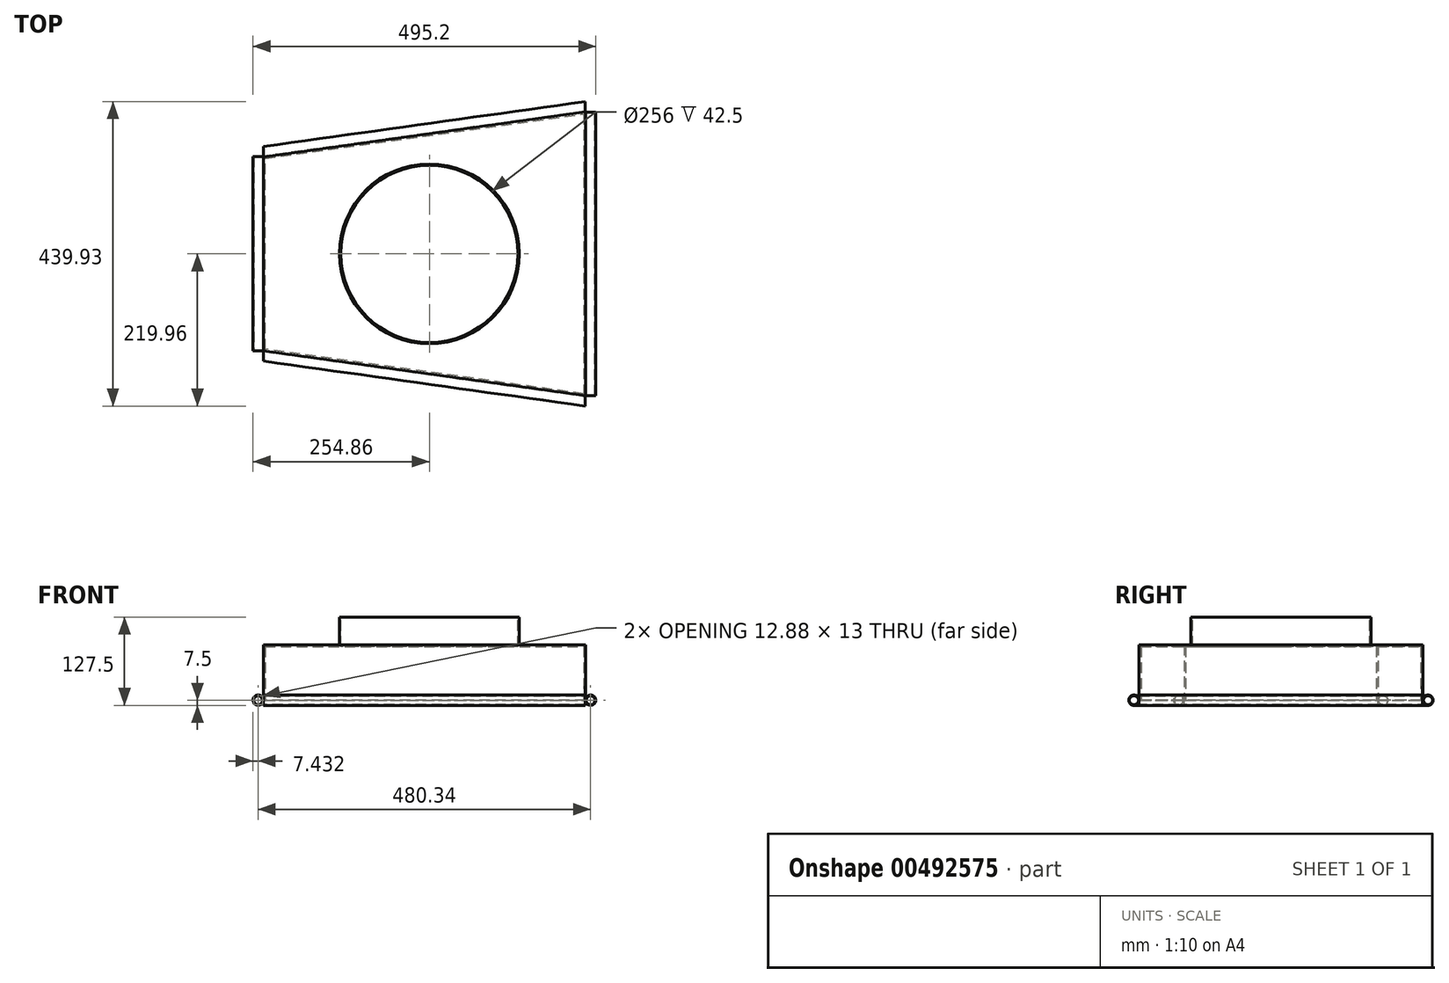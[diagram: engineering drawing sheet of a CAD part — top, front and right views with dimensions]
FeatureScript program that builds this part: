
annotation { "Feature Type Name" : "Feature", "Feature Type Description" : "" }
export const myFeature = defineFeature(function(context is Context, id is Id, definition is map)
    precondition{}
    {
        {
            var Q0;
            Q0=qCreatedBy(makeId("Top.planeOp"),FACE);
            var sketch = newSketch(context, id + "F0", { "sketchPlane" : qUnion([Q0])});
            skLineSegment(sketch, "E0", {"start": v(0, 0) * mm, "end": v(0, 280) * mm});
            skLineSegment(sketch, "E1", {"start": v(0, 140) * mm, "end": v(465.48, 140) * mm, "construction": true});
            skLineSegment(sketch, "E2", {"start": v(465.48, 345) * mm, "end": v(465.48, -65) * mm});
            skLineSegment(sketch, "E3", {"start": v(0, 280) * mm, "end": v(465.48, 345) * mm});
            skLineSegment(sketch, "E4", {"start": v(465.48, -65) * mm, "end": v(0, 0) * mm});
            skSolve(sketch);
        }
        {
            var Q0;
            Q0 = qSketchRegion(id + "F0", true);
            extrude(context, id + "F1", {"entities" : qUnion([Q0]), "depth" : 80 * mm, "offsetDistance" : 25 * mm});
        }
        {
            var Q0;
            Q0=makeQuery(id+"F1.opExtrude","CAP_FACE",FACE,{"disambiguationData":[OSD([sQuery(id+"F0.wireOp",EDGE,"E0"),sQuery(id+"F0.wireOp",EDGE,"E2"),sQuery(id+"F0.wireOp",EDGE,"E3"),sQuery(id+"F0.wireOp",EDGE,"E4")])],"isStart":false});
            var sketch = newSketch(context, id + "F2", { "sketchPlane" : qUnion([Q0])});
            skCircle(sketch, "E5", {"center": v(240, 140) * mm, "radius": 130 * mm});
            skLineSegment(sketch, "E6", {"start": v(465.48, 140) * mm, "end": v(0, 140) * mm, "construction": true});
            skSolve(sketch);
        }
        {
            var Q0;
            Q0 = qSketchRegion(id + "F2", true);
            extrude(context, id + "F3", {"entities" : qUnion([Q0]), "operationType" : NewBodyOperationType.ADD, "depth" : 40 * mm, "offsetDistance" : 25 * mm});
        }
        {
            var Q0;
            Q0=makeQuery(id+"F1.opExtrude","CAP_FACE",FACE,{"disambiguationData":[OSD([sQuery(id+"F0.wireOp",EDGE,"E0"),sQuery(id+"F0.wireOp",EDGE,"E2"),sQuery(id+"F0.wireOp",EDGE,"E3"),sQuery(id+"F0.wireOp",EDGE,"E4")])],"isStart":true});
            shell(context, id + "F4", {"entities" : qUnion([Q0]), "thickness" : 2.5 * mm});
        }
        {
            var Q0;
            Q0=makeQuery(id+"F3.opExtrude","CAP_FACE",FACE,{"disambiguationData":[OSD([sQuery(id+"F2.wireOp",EDGE,"E5")])],"isStart":false});
            var sketch = newSketch(context, id + "F5", { "sketchPlane" : qUnion([Q0])});
            skCircle(sketch, "E7.0", {"center": v(240, 140) * mm, "radius": 128 * mm});
            skSolve(sketch);
        }
        {
            var Q0;
            Q0 = qSketchRegion(id + "F5", true);
            var Q1;
            Q1=makeQuery(id+"F4.opShell","OFFSET_FACE",FACE,{"disambiguationData":[OSD([sQuery(id+"F0.wireOp",EDGE,"E0"),sQuery(id+"F0.wireOp",EDGE,"E2"),sQuery(id+"F0.wireOp",EDGE,"E3"),sQuery(id+"F0.wireOp",EDGE,"E4")])]});
            extrude(context, id + "F6", {"entities" : qUnion([Q0]), "operationType" : NewBodyOperationType.REMOVE, "endBound" : BoundingType.UP_TO_SURFACE, "oppositeDirection" : true, "depth" : 25 * mm, "endBoundEntityFace" : qUnion([Q1]), "offsetDistance" : 25 * mm});
        }
        {
            var Q0;
            Q0=makeQuery(id+"F1.opExtrude","SWEPT_FACE",FACE,{"disambiguationData":[OSD([sQuery(id+"F0.wireOp",EDGE,"E2")])]});
            var sketch = newSketch(context, id + "F7", { "sketchPlane" : qUnion([Q0])});
            skLineSegment(sketch, "E8", {"start": v(-65, 0) * mm, "end": v(-80, 0) * mm, "construction": true});
            skCircle(sketch, "E9", {"center": v(-72.5, 0) * mm, "radius": 7.5 * mm});
            skCircle(sketch, "E10.0", {"center": v(-72.5, 0) * mm, "radius": 6.5 * mm});
            skSolve(sketch);
        }
        {
            var Q0;
            Q0=qCreatedBy(makeId("Top.planeOp"),FACE);
            var sketch = newSketch(context, id + "F8", { "sketchPlane" : qUnion([Q0])});
            skLineSegment(sketch, "E11.0", {"start": v(-8, 286.96) * mm, "end": v(473.48, 354.2) * mm});
            skLineSegment(sketch, "E11.1", {"start": v(-8, -6.96) * mm, "end": v(-8, 286.96) * mm});
            skLineSegment(sketch, "E11.2", {"start": v(473.48, -74.2) * mm, "end": v(-8, -6.96) * mm});
            skLineSegment(sketch, "E11.3", {"start": v(473.48, 354.2) * mm, "end": v(473.48, -74.2) * mm});
            skSolve(sketch);
        }
        {
            var Q0;
            Q0=makeQuery(id+"F7.imprint","IMPRINT",FACE,{"disambiguationData":[TD([[makeQuery(id+"F7.imprint","IMPRINT",EDGE,{"derivedFrom":sQuery(id+"F7.wireOp",EDGE,"E9")}),1.0]])]});
            var Q1;
            Q1=sQuery(id+"F8.wireOp",EDGE,"E11.2");
            var Q2;
            Q2=sQuery(id+"F8.wireOp",EDGE,"E11.1");
            var Q3;
            Q3=sQuery(id+"F8.wireOp",EDGE,"E11.0");
            var Q4;
            Q4=sQuery(id+"F8.wireOp",EDGE,"E11.3");
            sweep(context, id + "F9", {"profiles" : qUnion([Q0]), "path" : qUnion([Q1, Q2, Q3, Q4])});
        }
        {
            var Q0;
            Q0=qCreatedBy(makeId("Top.planeOp"),FACE);
            var sketch = newSketch(context, id + "F10", { "sketchPlane" : qUnion([Q0])});
            skLineSegment(sketch, "E12.bottom", {"start": v(0, 0) * mm, "end": v(-35.78, 0) * mm});
            skLineSegment(sketch, "E12.top", {"start": v(0, -27.6) * mm, "end": v(-35.78, -27.6) * mm});
            skLineSegment(sketch, "E12.left", {"start": v(0, 0) * mm, "end": v(0, -27.6) * mm});
            skLineSegment(sketch, "E12.right", {"start": v(-35.78, 0) * mm, "end": v(-35.78, -27.6) * mm});
            skLineSegment(sketch, "E13.bottom", {"start": v(0, 280.38) * mm, "end": v(-35.78, 280.38) * mm});
            skLineSegment(sketch, "E13.top", {"start": v(0, 314.55) * mm, "end": v(-35.78, 314.55) * mm});
            skLineSegment(sketch, "E13.left", {"start": v(0, 280.38) * mm, "end": v(0, 314.55) * mm});
            skLineSegment(sketch, "E13.right", {"start": v(-35.78, 280.38) * mm, "end": v(-35.78, 314.55) * mm});
            skLineSegment(sketch, "E14.bottom", {"start": v(465.23, 344.53) * mm, "end": v(495.84, 344.53) * mm});
            skLineSegment(sketch, "E14.top", {"start": v(465.23, 377.57) * mm, "end": v(495.84, 377.57) * mm});
            skLineSegment(sketch, "E14.left", {"start": v(465.23, 344.53) * mm, "end": v(465.23, 377.57) * mm});
            skLineSegment(sketch, "E14.right", {"start": v(495.84, 344.53) * mm, "end": v(495.84, 377.57) * mm});
            skLineSegment(sketch, "E15.bottom", {"start": v(465.17, -64.94) * mm, "end": v(499.63, -64.94) * mm});
            skLineSegment(sketch, "E15.top", {"start": v(465.17, -93.86) * mm, "end": v(499.63, -93.86) * mm});
            skLineSegment(sketch, "E15.left", {"start": v(465.17, -64.94) * mm, "end": v(465.17, -93.86) * mm});
            skLineSegment(sketch, "E15.right", {"start": v(499.63, -64.94) * mm, "end": v(499.63, -93.86) * mm});
            skSolve(sketch);
        }
        {
            var Q0;
            Q0 = qSketchRegion(id + "F10", true);
            extrude(context, id + "F11", {"entities" : qUnion([Q0]), "operationType" : NewBodyOperationType.REMOVE, "endBound" : BoundingType.SYMMETRIC, "depth" : 40 * mm, "offsetDistance" : 25 * mm});
        }
    });
